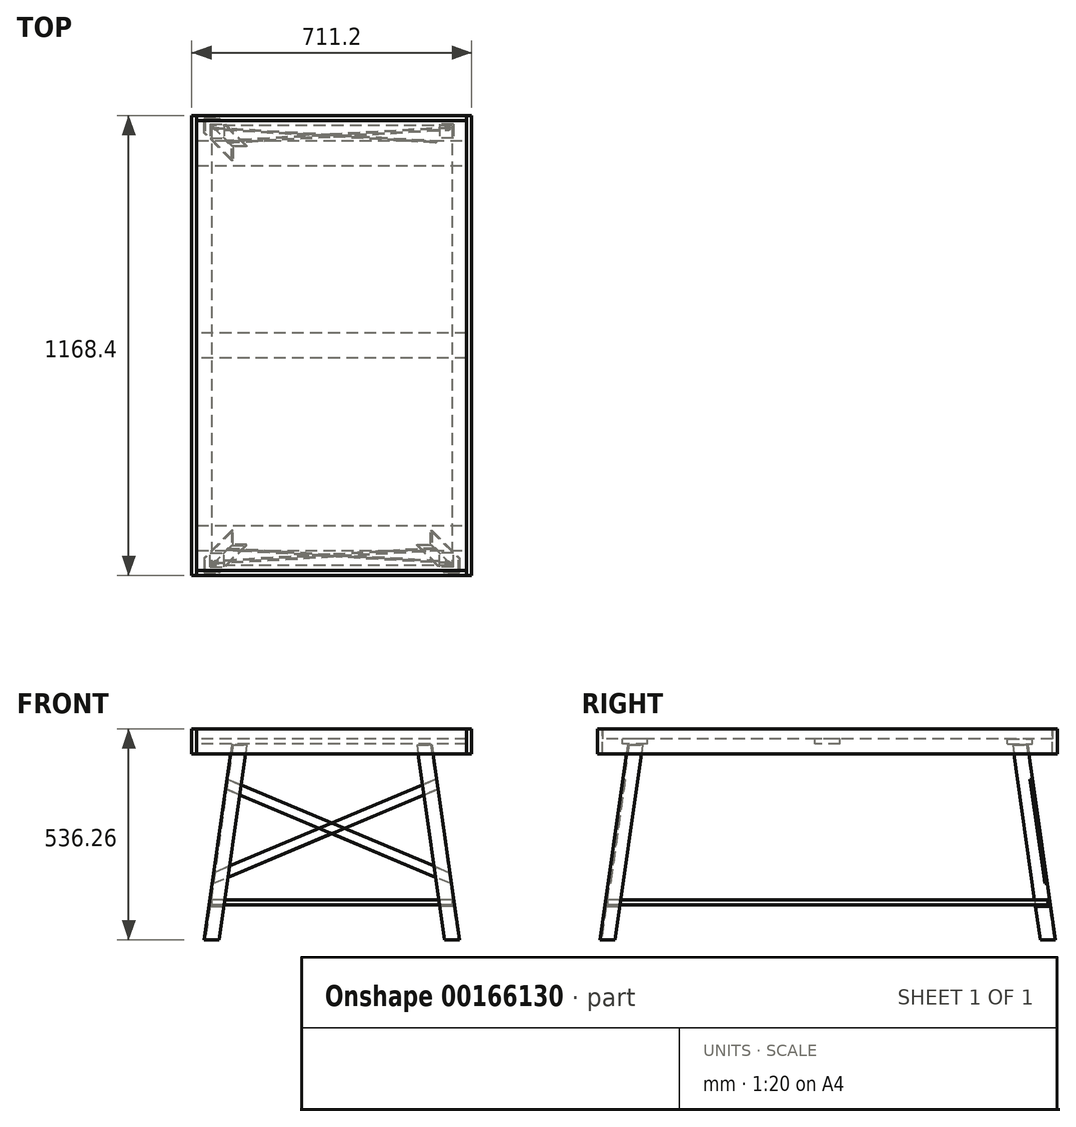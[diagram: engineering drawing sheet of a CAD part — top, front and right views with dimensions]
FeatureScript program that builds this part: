
annotation { "Feature Type Name" : "Feature", "Feature Type Description" : "" }
export const myFeature = defineFeature(function(context is Context, id is Id, definition is map)
    precondition{}
    {
        {
            var Q0;
            Q0=qCreatedBy(makeId("Top.planeOp"),FACE);
            var sketch = newSketch(context, id + "F0", { "sketchPlane" : qUnion([Q0])});
            skLineSegment(sketch, "E0.bottom", {"start": v(342.9, 571.5) * mm, "end": v(-342.9, 571.5) * mm});
            skLineSegment(sketch, "E0.top", {"start": v(342.9, -571.5) * mm, "end": v(-342.9, -571.5) * mm});
            skLineSegment(sketch, "E0.left", {"start": v(342.9, 571.5) * mm, "end": v(342.9, -571.5) * mm});
            skLineSegment(sketch, "E0.right", {"start": v(-342.9, 571.5) * mm, "end": v(-342.9, -571.5) * mm});
            skPoint(sketch, "E0.middle", {"position": v(0, 0) * mm});
            skSolve(sketch);
        }
        {
            var Q0;
            Q0 = qSketchRegion(id + "F0", true);
            extrude(context, id + "F1", {"entities" : qUnion([Q0]), "depth" : 25.4 * mm});
        }
        {
            var Q0;
            Q0=makeQuery(id+"F1.opExtrude","CAP_FACE",FACE,{"disambiguationData":[OSD([sQuery(id+"F0.wireOp",EDGE,"E0.bottom"),sQuery(id+"F0.wireOp",EDGE,"E0.top"),sQuery(id+"F0.wireOp",EDGE,"E0.left"),sQuery(id+"F0.wireOp",EDGE,"E0.right")])],"isStart":false});
            var sketch = newSketch(context, id + "F2", { "sketchPlane" : qUnion([Q0])});
            skLineSegment(sketch, "E1.bottom", {"start": v(-342.9, -571.5) * mm, "end": v(342.9, -571.5) * mm});
            skLineSegment(sketch, "E1.top", {"start": v(-342.9, -584.2) * mm, "end": v(342.9, -584.2) * mm});
            skLineSegment(sketch, "E1.left", {"start": v(-342.9, -571.5) * mm, "end": v(-342.9, -584.2) * mm});
            skLineSegment(sketch, "E1.right", {"start": v(342.9, -571.5) * mm, "end": v(342.9, -584.2) * mm});
            skLineSegment(sketch, "E2.bottom", {"start": v(-342.9, -584.2) * mm, "end": v(-355.6, -584.2) * mm});
            skLineSegment(sketch, "E2.top", {"start": v(-342.9, 584.2) * mm, "end": v(-355.6, 584.2) * mm});
            skLineSegment(sketch, "E2.left", {"start": v(-342.9, -584.2) * mm, "end": v(-342.9, 584.2) * mm});
            skLineSegment(sketch, "E2.right", {"start": v(-355.6, -584.2) * mm, "end": v(-355.6, 584.2) * mm});
            skSolve(sketch);
        }
        {
            var Q0;
            {var subQ0=sQuery(id+"F2.wireOp",EDGE,"E1.bottom");Q0=makeQuery(id+"F2.imprint","IMPRINT",FACE,{"disambiguationData":[TD([[makeQuery(id+"F2.imprint","IMPRINT",EDGE,{"derivedFrom":subQ0}),1.0]])]});}
            extrude(context, id + "F3", {"entities" : qUnion([Q0]), "oppositeDirection" : true, "depth" : 63.5 * mm});
        }
        {
            var Q0;
            {var subQ3=sQuery(id+"F2.wireOp",EDGE,"E2.bottom");Q0=makeQuery(id+"F2.imprint","IMPRINT",FACE,{"disambiguationData":[TD([[makeQuery(id+"F2.imprint","IMPRINT",EDGE,{"derivedFrom":subQ3}),-1.0]])]});}
            extrude(context, id + "F4", {"entities" : qUnion([Q0]), "oppositeDirection" : true, "depth" : 63.5 * mm});
        }
        {
            var Q0;
            Q0=makeQuery(id+"F4.opExtrude","SWEPT_BODY",BODY,{"disambiguationData":[OSD([sQuery(id+"F2.wireOp",EDGE,"E2.bottom"),sQuery(id+"F2.wireOp",EDGE,"E2.top"),sQuery(id+"F2.wireOp",EDGE,"E2.left"),sQuery(id+"F2.wireOp",EDGE,"E2.right")])]});
            var Q1;
            Q1=qCreatedBy(makeId("Right.planeOp"),FACE);
            mirror(context, id + "F5", {"entities" : qUnion([Q0]), "mirrorPlane" : qUnion([Q1])});
        }
        {
            var Q0;
            Q0=makeQuery(id+"F3.opExtrude","SWEPT_BODY",BODY,{"disambiguationData":[OSD([sQuery(id+"F2.wireOp",EDGE,"E1.bottom"),sQuery(id+"F2.wireOp",EDGE,"E1.top"),sQuery(id+"F2.wireOp",EDGE,"E1.right"),sQuery(id+"F2.wireOp",EDGE,"E2.left")])]});
            var Q1;
            Q1=qCreatedBy(makeId("Front.planeOp"),FACE);
            mirror(context, id + "F6", {"entities" : qUnion([Q0]), "mirrorPlane" : qUnion([Q1])});
        }
        {
            var Q0;
            Q0=makeQuery(id+"F1.opExtrude","CAP_FACE",FACE,{"disambiguationData":[OSD([sQuery(id+"F0.wireOp",EDGE,"E0.bottom"),sQuery(id+"F0.wireOp",EDGE,"E0.top"),sQuery(id+"F0.wireOp",EDGE,"E0.left"),sQuery(id+"F0.wireOp",EDGE,"E0.right")])],"isStart":true});
            var sketch = newSketch(context, id + "F7", { "sketchPlane" : qUnion([Q0])});
            skLineSegment(sketch, "E3.bottom", {"start": v(-342.9, 520.7) * mm, "end": v(342.9, 520.7) * mm});
            skLineSegment(sketch, "E3.top", {"start": v(-342.9, 457.2) * mm, "end": v(342.9, 457.2) * mm});
            skLineSegment(sketch, "E3.left", {"start": v(-342.9, 520.7) * mm, "end": v(-342.9, 457.2) * mm});
            skLineSegment(sketch, "E3.right", {"start": v(342.9, 520.7) * mm, "end": v(342.9, 457.2) * mm});
            skLineSegment(sketch, "E4.bottom", {"start": v(342.9, -31.75) * mm, "end": v(-342.9, -31.75) * mm});
            skLineSegment(sketch, "E4.top", {"start": v(342.9, 31.75) * mm, "end": v(-342.9, 31.75) * mm});
            skLineSegment(sketch, "E4.left", {"start": v(342.9, -31.75) * mm, "end": v(342.9, 31.75) * mm});
            skLineSegment(sketch, "E4.right", {"start": v(-342.9, -31.75) * mm, "end": v(-342.9, 31.75) * mm});
            skPoint(sketch, "E4.middle", {"position": v(0, 0) * mm});
            skSolve(sketch);
        }
        {
            var Q0;
            Q0 = qSketchRegion(id + "F7", true);
            extrude(context, id + "F8", {"entities" : qUnion([Q0]), "depth" : 12.7 * mm});
        }
        {
            var Q0;
            Q0=makeQuery(id+"F8.opExtrude","CAP_FACE",FACE,{"disambiguationData":[OSD([sQuery(id+"F7.wireOp",EDGE,"E3.bottom"),sQuery(id+"F7.wireOp",EDGE,"E3.top"),sQuery(id+"F7.wireOp",EDGE,"E3.left"),sQuery(id+"F7.wireOp",EDGE,"E3.right")])],"isStart":false});
            var sketch = newSketch(context, id + "F9", { "sketchPlane" : qUnion([Q0])});
            skLineSegment(sketch, "E5", {"start": v(-254, 469.9) * mm, "end": v(-254, 508) * mm});
            skLineSegment(sketch, "E6", {"start": v(-254, 508) * mm, "end": v(-215.9, 508) * mm});
            skLineSegment(sketch, "E7", {"start": v(-215.9, 508) * mm, "end": v(-215.9, 504.82) * mm});
            skLineSegment(sketch, "E8", {"start": v(-215.9, 504.82) * mm, "end": v(-250.83, 504.82) * mm});
            skLineSegment(sketch, "E9", {"start": v(-250.83, 504.82) * mm, "end": v(-250.83, 469.9) * mm});
            skLineSegment(sketch, "E10", {"start": v(-250.83, 469.9) * mm, "end": v(-254, 469.9) * mm});
            skLineSegment(sketch, "E11", {"start": v(-254, 488.95) * mm, "end": v(-342.9, 488.95) * mm, "construction": true});
            skSolve(sketch);
        }
        {
            var Q0;
            Q0=sQuery(id+"F9.wireOp",EDGE,"E6");
            var Q1;
            Q1=makeQuery(id+"F9.imprint","IMPRINT",FACE,{"disambiguationData":[TD([[makeQuery(id+"F9.imprint","IMPRINT",EDGE,{"derivedFrom":sQuery(id+"F9.wireOp",EDGE,"E5")}),1.0]])]});
            cPlane(context, id + "F10", {"entities" : qUnion([Q0, Q1]), "cplaneType" : CPlaneType.LINE_ANGLE, "offset" : 25.4 * mm, "angle" : 82 * degree, "width" : 152.4 * mm, "height" : 152.4 * mm});
        }
        {
            var Q0;
            Q0=qCreatedBy(id+"F10.planeOp",FACE);
            var sketch = newSketch(context, id + "F11", { "sketchPlane" : qUnion([Q0])});
            skLineSegment(sketch, "E12", {"start": v(-254, -83.28) * mm, "end": v(-324.7, -586.33) * mm});
            skLineSegment(sketch, "E13", {"start": v(-254, -83.28) * mm, "end": v(-254, -459.38) * mm, "construction": true});
            skSolve(sketch);
        }
        {
            var Q0;
            Q0=makeQuery(id+"F9.imprint","IMPRINT",FACE,{"disambiguationData":[TD([[makeQuery(id+"F9.imprint","IMPRINT",EDGE,{"derivedFrom":sQuery(id+"F9.wireOp",EDGE,"E5")}),-1.0]])]});
            var Q1;
            Q1=sQuery(id+"F11.wireOp",EDGE,"E12");
            sweep(context, id + "F12", {"profiles" : qUnion([Q0]), "path" : qUnion([Q1])});
        }
        {
            var Q0;
            Q0=makeQuery(id+"F8.opExtrude","CAP_FACE",FACE,{"disambiguationData":[OSD([sQuery(id+"F7.wireOp",EDGE,"E3.bottom"),sQuery(id+"F7.wireOp",EDGE,"E3.top"),sQuery(id+"F7.wireOp",EDGE,"E3.left"),sQuery(id+"F7.wireOp",EDGE,"E3.right")])],"isStart":false});
            var sketch = newSketch(context, id + "F13", { "sketchPlane" : qUnion([Q0])});
            skLineSegment(sketch, "E14.bottom", {"start": v(304.8, 514.35) * mm, "end": v(-304.8, 514.35) * mm});
            skLineSegment(sketch, "E14.top", {"start": v(304.8, 463.55) * mm, "end": v(-304.8, 463.55) * mm});
            skLineSegment(sketch, "E14.left", {"start": v(304.8, 514.35) * mm, "end": v(304.8, 463.55) * mm});
            skLineSegment(sketch, "E14.right", {"start": v(-304.8, 514.35) * mm, "end": v(-304.8, 463.55) * mm});
            skLineSegment(sketch, "E15", {"start": v(0, 463.55) * mm, "end": v(0, 0) * mm, "construction": true});
            skLineSegment(sketch, "E16", {"start": v(342.9, 488.95) * mm, "end": v(304.8, 488.95) * mm, "construction": true});
            skPoint(sketch, "E16.endSnap0", {"position": v(304.8, 488.95) * mm});
            skSolve(sketch);
        }
        {
            var Q0;
            Q0 = qSketchRegion(id + "F13", true);
            extrude(context, id + "F14", {"entities" : qUnion([Q0]), "depth" : 3.17 * mm});
        }
        {
            var Q0;
            Q0 = qSketchRegion(id + "F13", true);
            extrude(context, id + "F15", {"entities" : qUnion([Q0]), "operationType" : NewBodyOperationType.REMOVE, "depth" : 3.17 * mm});
        }
        {
            var Q0;
            Q0=makeQuery(id+"F12.opSweep","SWEPT_BODY",BODY,{"disambiguationData":[OSD([sQuery(id+"F9.wireOp",EDGE,"E5"),sQuery(id+"F9.wireOp",EDGE,"E6"),sQuery(id+"F9.wireOp",EDGE,"E7"),sQuery(id+"F9.wireOp",EDGE,"E8"),sQuery(id+"F9.wireOp",EDGE,"E9"),sQuery(id+"F9.wireOp",EDGE,"E10"),sQuery(id+"F11.wireOp",EDGE,"E12")])]});
            var Q1;
            Q1=qCreatedBy(makeId("Right.planeOp"),FACE);
            mirror(context, id + "F16", {"operationType" : NewBodyOperationType.ADD, "entities" : qUnion([Q0]), "mirrorPlane" : qUnion([Q1])});
        }
        {
            var Q0;
            Q0=makeQuery(id+"F16.opPattern","COPY",FACE,{"derivedFrom":makeQuery(id+"F12.opSweep","SWEPT_FACE",FACE,{"disambiguationData":[OSD([sQuery(id+"F9.wireOp",EDGE,"E8"),sQuery(id+"F11.wireOp",EDGE,"E12")])]}),"instanceName":"1"});
            var sketch = newSketch(context, id + "F17", { "sketchPlane" : qUnion([Q0])});
            skLineSegment(sketch, "E17", {"start": v(-263.65, -174.08) * mm, "end": v(297.1, -412.1) * mm});
            skLineSegment(sketch, "E18", {"start": v(297.1, -412.1) * mm, "end": v(301.08, -440.44) * mm});
            skLineSegment(sketch, "E19", {"start": v(301.08, -440.44) * mm, "end": v(-267.18, -199.23) * mm});
            skLineSegment(sketch, "E20", {"start": v(-267.18, -199.23) * mm, "end": v(-263.65, -174.08) * mm});
            skSolve(sketch);
        }
        {
            var Q0;
            Q0 = qSketchRegion(id + "F17", true);
            extrude(context, id + "F18", {"entities" : qUnion([Q0]), "depth" : 3.17 * mm});
        }
        {
            var Q0;
            Q0=makeQuery(id+"F18.opExtrude","SWEPT_BODY",BODY,{"disambiguationData":[OSD([sQuery(id+"F17.wireOp",EDGE,"E17"),sQuery(id+"F17.wireOp",EDGE,"E18"),sQuery(id+"F17.wireOp",EDGE,"E19"),sQuery(id+"F17.wireOp",EDGE,"E20")])]});
            var Q1;
            Q1=qCreatedBy(makeId("Right.planeOp"),FACE);
            mirror(context, id + "F19", {"entities" : qUnion([Q0]), "mirrorPlane" : qUnion([Q1])});
        }
        {
            var Q0;
            Q0=makeQuery(id+"F16.opPattern","COPY",FACE,{"derivedFrom":makeQuery(id+"F12.opSweep","CAP_FACE",FACE,{"disambiguationData":[OSD([sQuery(id+"F9.wireOp",EDGE,"E5"),sQuery(id+"F9.wireOp",EDGE,"E6"),sQuery(id+"F9.wireOp",EDGE,"E7"),sQuery(id+"F9.wireOp",EDGE,"E8"),sQuery(id+"F9.wireOp",EDGE,"E9"),sQuery(id+"F9.wireOp",EDGE,"E10"),sQuery(id+"F11.wireOp",VERTEX,"E12.end")])],"isStart":false}),"instanceName":"1"});
            cPlane(context, id + "F20", {"entities" : qUnion([Q0]), "cplaneType" : CPlaneType.OFFSET, "offset" : 88.9 * mm, "oppositeDirection" : true, "width" : 152.4 * mm, "height" : 152.4 * mm});
        }
        {
            var Q0;
            Q0=qCreatedBy(id+"F20.planeOp",FACE);
            var sketch = newSketch(context, id + "F21", { "sketchPlane" : qUnion([Q0])});
            skLineSegment(sketch, "E21.bottom", {"start": v(308.9, 562.34) * mm, "end": v(273.98, 562.34) * mm});
            skLineSegment(sketch, "E21.top", {"start": v(308.9, 527.42) * mm, "end": v(273.98, 527.42) * mm});
            skLineSegment(sketch, "E21.left", {"start": v(308.9, 562.34) * mm, "end": v(308.9, 527.42) * mm});
            skLineSegment(sketch, "E21.right", {"start": v(273.98, 562.34) * mm, "end": v(273.98, 527.42) * mm});
            skSolve(sketch);
        }
        {
            var Q0;
            Q0 = qSketchRegion(id + "F21", true);
            extrude(context, id + "F22", {"entities" : qUnion([Q0]), "depth" : 3.17 * mm});
        }
        {
            var Q0;
            Q0=makeQuery(id+"F22.opExtrude","SWEPT_BODY",BODY,{"disambiguationData":[OSD([sQuery(id+"F21.wireOp",EDGE,"E21.bottom"),sQuery(id+"F21.wireOp",EDGE,"E21.top"),sQuery(id+"F21.wireOp",EDGE,"E21.left"),sQuery(id+"F21.wireOp",EDGE,"E21.right")])]});
            var Q1;
            Q1=qCreatedBy(makeId("Right.planeOp"),FACE);
            mirror(context, id + "F23", {"entities" : qUnion([Q0]), "mirrorPlane" : qUnion([Q1])});
        }
        {
            var Q0;
            Q0=makeQuery(id+"F8.opExtrude","SWEPT_BODY",BODY,{"disambiguationData":[OSD([sQuery(id+"F7.wireOp",EDGE,"E3.bottom"),sQuery(id+"F7.wireOp",EDGE,"E3.top"),sQuery(id+"F7.wireOp",EDGE,"E3.left"),sQuery(id+"F7.wireOp",EDGE,"E3.right")])]});
            var Q1;
            Q1=makeQuery(id+"F12.opSweep","SWEPT_BODY",BODY,{"disambiguationData":[OSD([sQuery(id+"F9.wireOp",EDGE,"E5"),sQuery(id+"F9.wireOp",EDGE,"E6"),sQuery(id+"F9.wireOp",EDGE,"E7"),sQuery(id+"F9.wireOp",EDGE,"E8"),sQuery(id+"F9.wireOp",EDGE,"E9"),sQuery(id+"F9.wireOp",EDGE,"E10"),sQuery(id+"F11.wireOp",EDGE,"E12")])]});
            var Q2;
            Q2=makeQuery(id+"F19.opPattern","COPY",BODY,{"derivedFrom":makeQuery(id+"F18.opExtrude","SWEPT_BODY",BODY,{"disambiguationData":[OSD([sQuery(id+"F17.wireOp",EDGE,"E17"),sQuery(id+"F17.wireOp",EDGE,"E18"),sQuery(id+"F17.wireOp",EDGE,"E19"),sQuery(id+"F17.wireOp",EDGE,"E20")])]}),"instanceName":"1"});
            var Q3;
            Q3=makeQuery(id+"F18.opExtrude","SWEPT_BODY",BODY,{"disambiguationData":[OSD([sQuery(id+"F17.wireOp",EDGE,"E17"),sQuery(id+"F17.wireOp",EDGE,"E18"),sQuery(id+"F17.wireOp",EDGE,"E19"),sQuery(id+"F17.wireOp",EDGE,"E20")])]});
            var Q4;
            Q4=makeQuery(id+"F23.opPattern","COPY",BODY,{"derivedFrom":makeQuery(id+"F22.opExtrude","SWEPT_BODY",BODY,{"disambiguationData":[OSD([sQuery(id+"F21.wireOp",EDGE,"E21.bottom"),sQuery(id+"F21.wireOp",EDGE,"E21.top"),sQuery(id+"F21.wireOp",EDGE,"E21.left"),sQuery(id+"F21.wireOp",EDGE,"E21.right")])]}),"instanceName":"1"});
            var Q5;
            Q5=makeQuery(id+"F22.opExtrude","SWEPT_BODY",BODY,{"disambiguationData":[OSD([sQuery(id+"F21.wireOp",EDGE,"E21.bottom"),sQuery(id+"F21.wireOp",EDGE,"E21.top"),sQuery(id+"F21.wireOp",EDGE,"E21.left"),sQuery(id+"F21.wireOp",EDGE,"E21.right")])]});
            var Q6;
            Q6=qCreatedBy(makeId("Front.planeOp"),FACE);
            mirror(context, id + "F24", {"entities" : qUnion([Q0, Q1, Q2, Q3, Q4, Q5]), "mirrorPlane" : qUnion([Q6])});
        }
        {
            var Q0;
            Q0=makeQuery(id+"F22.opExtrude","CAP_FACE",FACE,{"disambiguationData":[OSD([sQuery(id+"F21.wireOp",EDGE,"E21.bottom"),sQuery(id+"F21.wireOp",EDGE,"E21.top"),sQuery(id+"F21.wireOp",EDGE,"E21.left"),sQuery(id+"F21.wireOp",EDGE,"E21.right")])],"isStart":true});
            var sketch = newSketch(context, id + "F25", { "sketchPlane" : qUnion([Q0])});
            skLineSegment(sketch, "E22.bottom", {"start": v(305.73, 559.17) * mm, "end": v(-305.73, 559.17) * mm});
            skLineSegment(sketch, "E22.top", {"start": v(305.73, -559.17) * mm, "end": v(-305.73, -559.17) * mm});
            skLineSegment(sketch, "E22.left", {"start": v(305.73, 559.17) * mm, "end": v(305.73, -559.17) * mm});
            skLineSegment(sketch, "E22.right", {"start": v(-305.73, 559.17) * mm, "end": v(-305.73, -559.17) * mm});
            skSolve(sketch);
        }
        {
            var Q0;
            Q0 = qSketchRegion(id + "F25", true);
            extrude(context, id + "F26", {"entities" : qUnion([Q0]), "depth" : 12.7 * mm});
        }
    });
